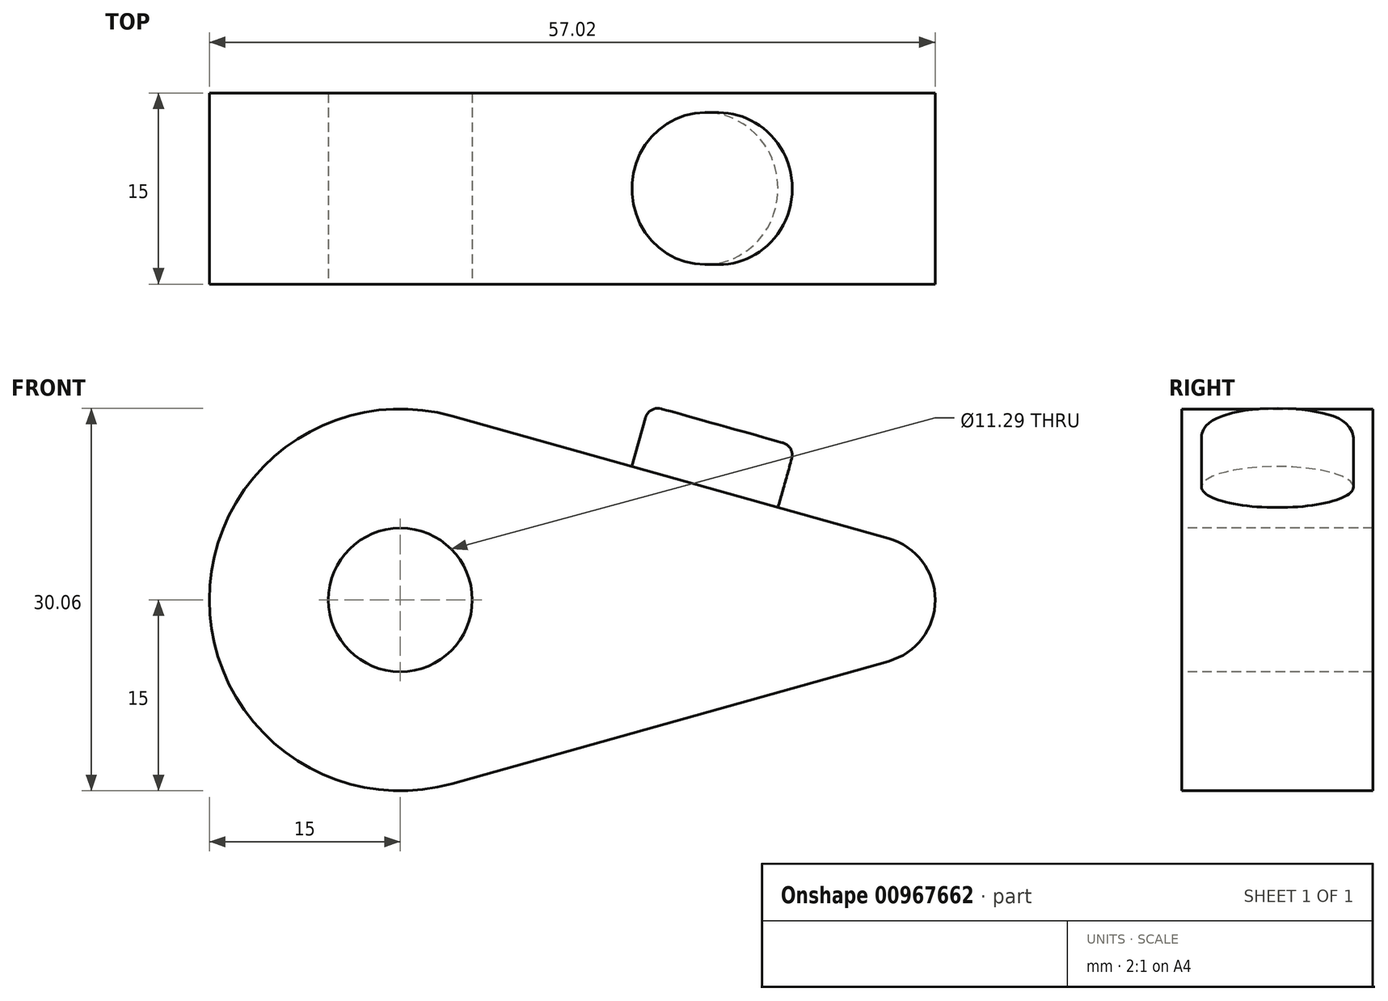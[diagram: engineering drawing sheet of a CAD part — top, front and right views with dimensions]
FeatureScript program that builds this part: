
annotation { "Feature Type Name" : "Feature", "Feature Type Description" : "" }
export const myFeature = defineFeature(function(context is Context, id is Id, definition is map)
    precondition{}
    {
        {
            var Q0;
            Q0=qCreatedBy(makeId("Front.planeOp"),FACE);
            var sketch = newSketch(context, id + "F0", { "sketchPlane" : qUnion([Q0])});
            skCircle(sketch, "E0", {"center": v(0, 0) * mm, "radius": 15 * mm});
            skCircle(sketch, "E1", {"center": v(37.02, 0) * mm, "radius": 5 * mm});
            skLineSegment(sketch, "E2", {"start": v(4.05, 14.44) * mm, "end": v(38.37, 4.81) * mm});
            skLineSegment(sketch, "E3", {"start": v(4.05, -14.44) * mm, "end": v(38.37, -4.81) * mm});
            skSolve(sketch);
        }
        {
            var Q0;
            Q0 = qSketchRegion(id + "F0", true);
            extrude(context, id + "F1", {"entities" : qUnion([Q0]), "depth" : 15 * mm, "offsetDistance" : 25.4 * mm});
        }
        {
            var Q0;
            Q0=makeQuery(id+"F1.opExtrude","CAP_FACE",FACE,{"disambiguationData":[OSD([sQuery(id+"F0.wireOp",EDGE,"E0"),sQuery(id+"F0.wireOp",EDGE,"E1"),sQuery(id+"F0.wireOp",EDGE,"E2"),sQuery(id+"F0.wireOp",EDGE,"E3")])],"isStart":false});
            var sketch = newSketch(context, id + "F2", { "sketchPlane" : qUnion([Q0])});
            skCircle(sketch, "E4", {"center": v(0, 0) * mm, "radius": 5.65 * mm});
            skSolve(sketch);
        }
        {
            var Q0;
            Q0 = qSketchRegion(id + "F2", true);
            extrude(context, id + "F3", {"entities" : qUnion([Q0]), "operationType" : NewBodyOperationType.REMOVE, "oppositeDirection" : true, "depth" : 16 * mm, "offsetDistance" : 25.4 * mm});
        }
        {
            var Q0;
            Q0=makeQuery(id+"F1.opExtrude","SWEPT_FACE",FACE,{"disambiguationData":[OSD([sQuery(id+"F0.wireOp",EDGE,"E2")])]});
            var sketch = newSketch(context, id + "F4", { "sketchPlane" : qUnion([Q0])});
            skCircle(sketch, "E5", {"center": v(20.65, -7.5) * mm, "radius": 5.96 * mm});
            skPoint(sketch, "E5.centerSnap0", {"position": v(35.64, -7.5) * mm});
            skSolve(sketch);
        }
        {
            var Q0;
            Q0 = qSketchRegion(id + "F4", true);
            extrude(context, id + "F5", {"entities" : qUnion([Q0]), "operationType" : NewBodyOperationType.ADD, "depth" : 5 * mm, "offsetDistance" : 25.4 * mm});
        }
        {
            var Q0;
            Q0=makeQuery(id+"F5.opExtrude","CAP_EDGE",EDGE,{"disambiguationData":[OSD([sQuery(id+"F4.wireOp",EDGE,"E5")])],"isStart":false});
            var Q1;
            Q1=makeQuery(id+"F5.opExtrude","CAP_EDGE",EDGE,{"disambiguationData":[OSD([sQuery(id+"F4.wireOp",EDGE,"E5")])],"isStart":true});
            fillet(context, id + "F6", {"entities" : qUnion([Q0, Q1]), "radius" : 1 * mm, "tangentPropagation" : true, "allowEdgeOverflow" : false});
        }
    });
